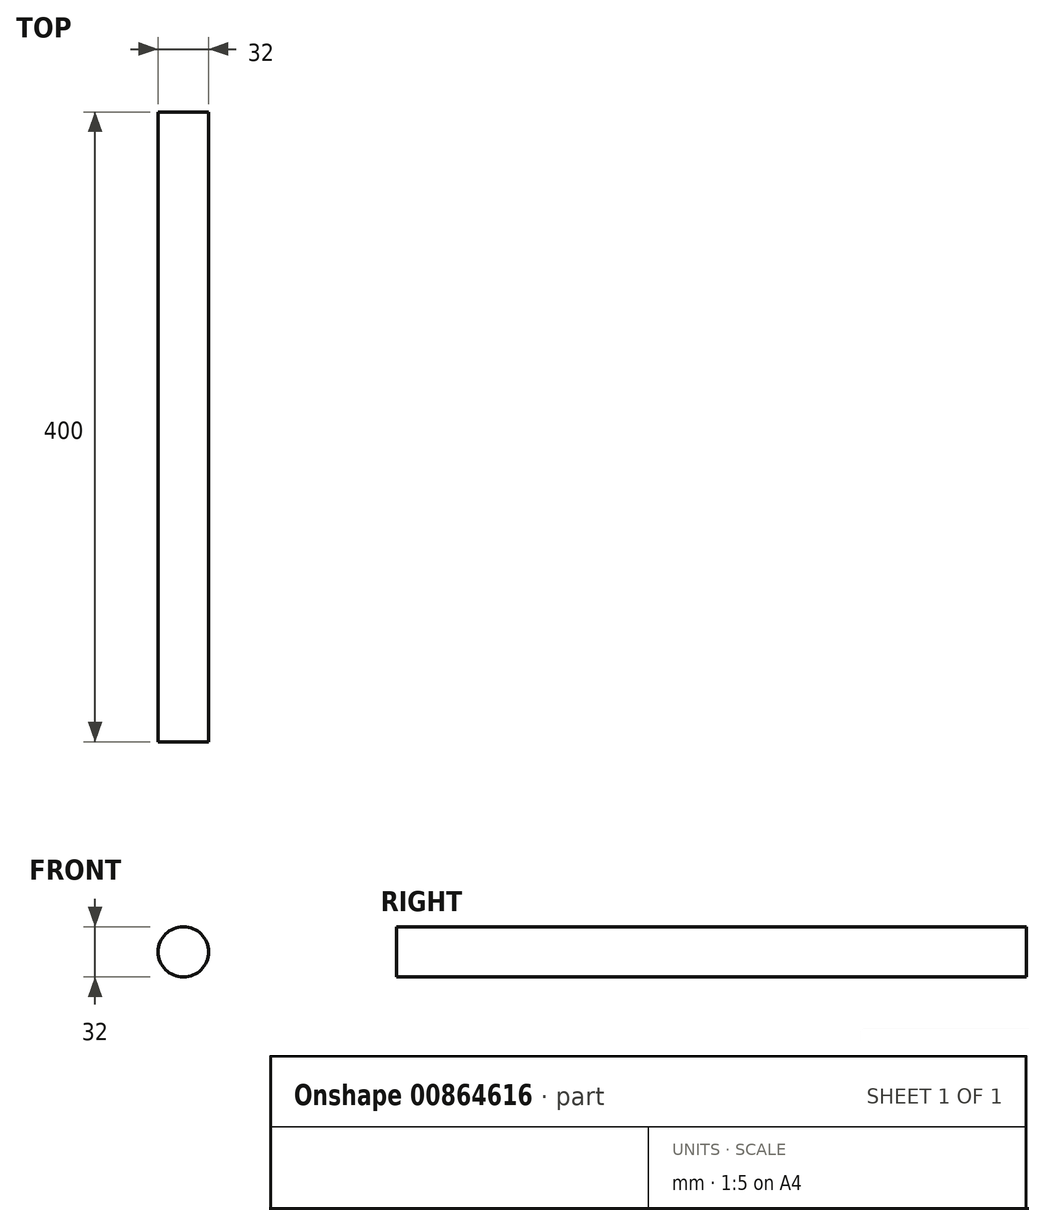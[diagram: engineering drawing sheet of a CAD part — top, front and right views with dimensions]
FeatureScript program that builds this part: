
annotation { "Feature Type Name" : "Feature", "Feature Type Description" : "" }
export const myFeature = defineFeature(function(context is Context, id is Id, definition is map)
    precondition{}
    {
        {
            var Q0;
            Q0=qCreatedBy(makeId("Front.planeOp"),FACE);
            var sketch = newSketch(context, id + "F0", { "sketchPlane" : qUnion([Q0])});
            skCircle(sketch, "E0", {"center": v(0, 0) * mm, "radius": 16 * mm});
            skSolve(sketch);
        }
        {
            var Q0;
            Q0 = qSketchRegion(id + "F0", true);
            extrude(context, id + "F1", {"entities" : qUnion([Q0]), "depth" : 400 * mm, "offsetDistance" : 25 * mm});
        }
    });
